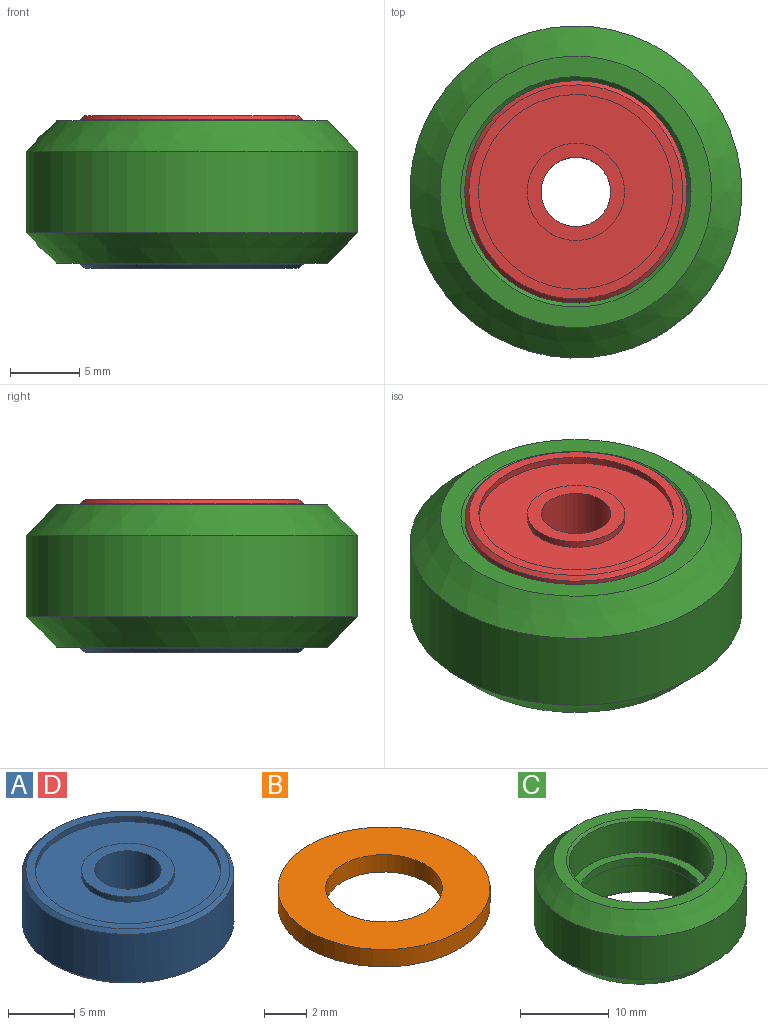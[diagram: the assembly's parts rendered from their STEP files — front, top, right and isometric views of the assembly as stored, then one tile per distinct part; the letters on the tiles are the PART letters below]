
ASSEMBLY  parts=4 mates=3
PART A: 14 faces, bbox 16x16x5 mm
  f0: cylinder r=8mm len=16mm, axis (0,0,-1), area 221.2mm2, adj f12,f13
  f1: plane 15.4x15.4mm, normal (0,0,1), area 32.3mm2, adj f2,f13
  f2: cylinder r=7mm len=14mm, axis (0,0,1), area 22mm2, adj f1,f3
  f3: plane 14x14mm, normal (0,0,1), area 115.5mm2, adj f2,f4
  f4: cylinder r=3.5mm len=7mm, axis (0,0,-1), area 11mm2, adj f3,f5
  f5: plane 7x7mm, normal (0,0,1), area 18.8mm2, adj f4,f6
  f6: cylinder r=2.5mm len=5mm, axis (0,0,1), area 78.5mm2, adj f5,f11
  f7: plane 15.4x15.4mm, normal (0,0,-1), area 32.3mm2, adj f8,f12
  f8: cylinder r=7mm len=14mm, axis (0,0,-1), area 22mm2, adj f7,f9
  f9: plane 14x14mm, normal (0,0,-1), area 115.5mm2, adj f8,f10
  f10: cylinder r=3.5mm len=7mm, axis (0,0,1), area 11mm2, adj f9,f11
  f11: plane 7x7mm, normal (0,0,-1), area 18.8mm2, adj f6,f10
  f12: cone r=8mm half-angle=45deg, axis (0,0,1), area 20.9mm2, adj f0,f7
  f13: cone r=7.7mm half-angle=45deg, axis (0,0,-1), area 20.9mm2, adj f0,f1
PART B: 4 faces, bbox 10x10x1 mm
  f0: cylinder r=2.75mm len=5.5mm, axis (0,0,-1), area 17.3mm2, adj f2,f3
  f1: cylinder r=5mm len=10mm, axis (0,0,-1), area 31.4mm2, adj f2,f3
  f2: plane 10x10mm, normal (0,0,1), area 54.8mm2, adj f0,f1
  f3: plane 10x10mm, normal (0,0,-1), area 54.8mm2, adj f0,f1
PART C: 12 faces, bbox 23.9x23.9x10.2 mm
  f0: cylinder r=11.95mm len=23.89mm, axis (0,0,-1), area 442.1mm2, adj f2,f8
  f1: plane 19.54x19.54mm, normal (0,0,-1), area 84.1mm2, adj f2,f6
  f2: cone r=11.95mm half-angle=45deg, axis (0,0,1), area 209.8mm2, adj f0,f1
  f3: cylinder r=7.99mm len=15.97mm, axis (0,0,-1), area 216.8mm2, adj f4,f6
  f4: plane 15.97x15.97mm, normal (0,0,-1), area 48.9mm2, adj f3,f5
  f5: cylinder r=6.94mm len=13.89mm, axis (0,0,-1), area 43.6mm2, adj f4,f10
  f6: cone r=7.99mm half-angle=45deg, axis (0,0,-1), area 21.7mm2, adj f1,f3
  f7: plane 19.54x19.54mm, normal (0,0,1), area 84.1mm2, adj f8,f11
  f8: cone r=11.95mm half-angle=45deg, axis (0,0,-1), area 209.8mm2, adj f0,f7
  f9: cylinder r=7.99mm len=15.97mm, axis (0,0,1), area 216.8mm2, adj f10,f11
  f10: plane 15.97x15.97mm, normal (0,0,1), area 48.9mm2, adj f5,f9
  f11: cone r=7.99mm half-angle=45deg, axis (0,0,1), area 21.7mm2, adj f7,f9
PART D: same geometry as A
PLACE A rot(axis=(1,0,0),180deg) t=(0,0,-3)mm
PLACE B t=(0,0,-0.5)mm
PLACE C t=(0,0,-5.12)mm
PLACE D rot(axis=(1,0,0),180deg) t=(0,0,3)mm
MATE fastened A.f0 <-> B.f0  axis (0,0,1) through (0,0,-0.5)mm
MATE fastened C.f0 <-> B.f0  axis (0,0,-1) through (0,0,0)mm
MATE fastened D.f0 <-> B.f0  axis (0,0,-1) through (0,0,0.5)mm
